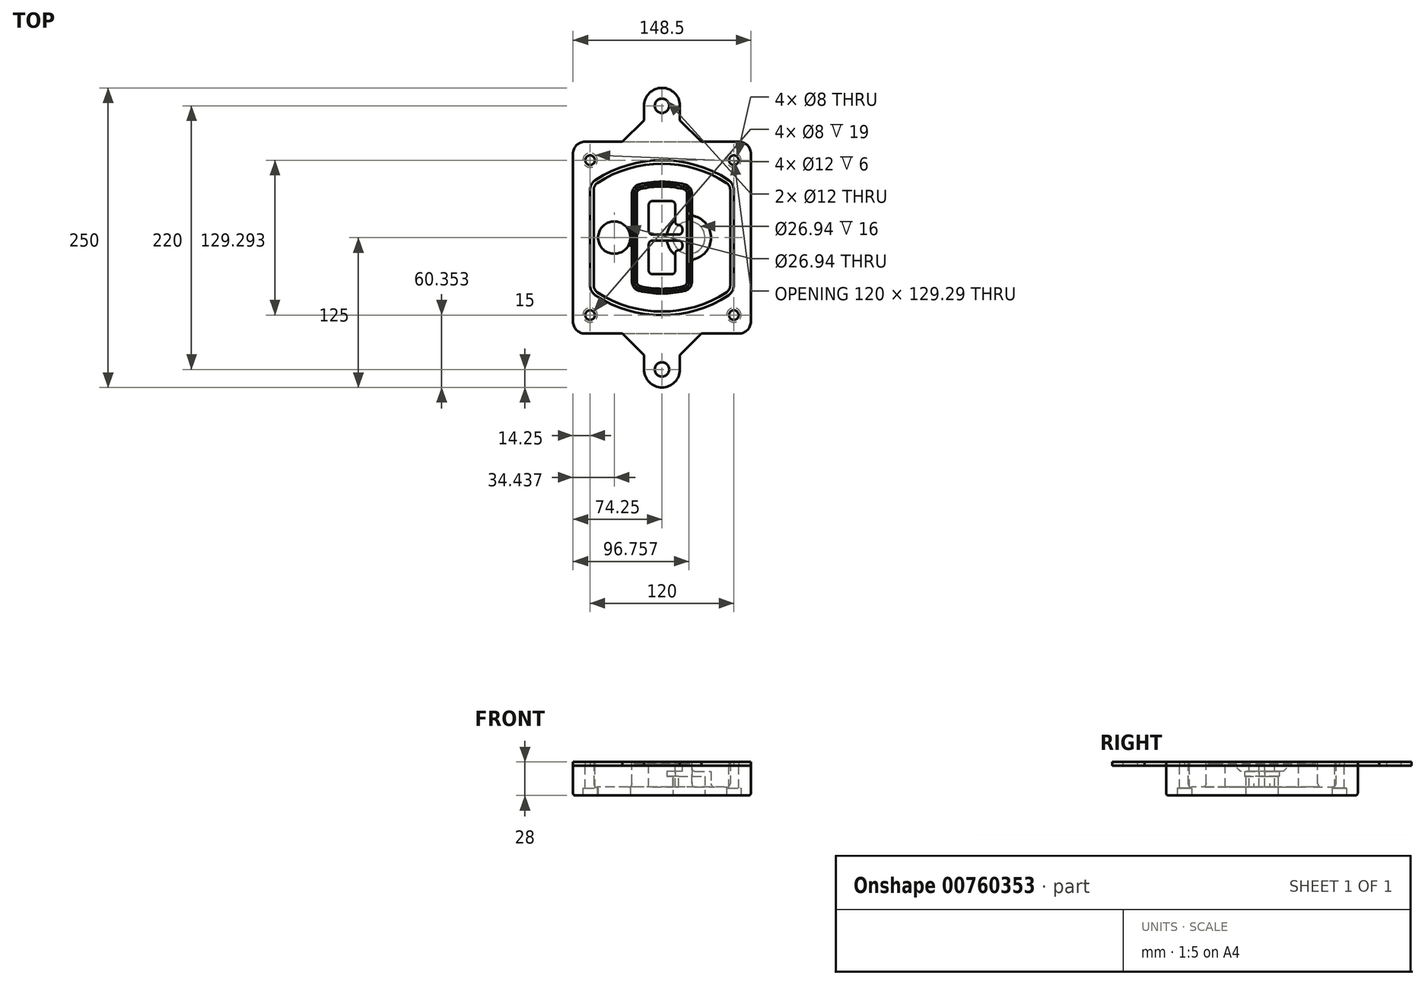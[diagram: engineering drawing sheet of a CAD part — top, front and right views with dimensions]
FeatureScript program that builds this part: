
annotation { "Feature Type Name" : "Feature", "Feature Type Description" : "" }
export const myFeature = defineFeature(function(context is Context, id is Id, definition is map)
    precondition{}
    {
        {
            var Q0;
            Q0=qCreatedBy(makeId("Top.planeOp"),FACE);
            var sketch = newSketch(context, id + "F0", { "sketchPlane" : qUnion([Q0])});
            skPoint(sketch, "E0.rect.middle", {"position": v(0, 0) * mm});
            skLineSegment(sketch, "E1.bottom", {"start": v(-64.25, -80) * mm, "end": v(64.25, -80) * mm});
            skLineSegment(sketch, "E1.top", {"start": v(-64.25, 80) * mm, "end": v(64.25, 80) * mm});
            skLineSegment(sketch, "E1.left", {"start": v(-74.25, -70) * mm, "end": v(-74.25, 70) * mm});
            skLineSegment(sketch, "E1.right", {"start": v(74.25, -70) * mm, "end": v(74.25, 70) * mm});
            skLineSegment(sketch, "E2", {"start": v(-74.25, 80) * mm, "end": v(74.25, -80) * mm, "construction": true});
            skLineSegment(sketch, "E3", {"start": v(74.25, 80) * mm, "end": v(-74.25, -80) * mm, "construction": true});
            skCircle(sketch, "E4", {"center": v(-60, 64.65) * mm, "radius": 4 * mm});
            skCircle(sketch, "E5", {"center": v(60, 64.65) * mm, "radius": 4 * mm});
            skCircle(sketch, "E6", {"center": v(60, -64.65) * mm, "radius": 4 * mm});
            skCircle(sketch, "E7", {"center": v(-60, -64.65) * mm, "radius": 4 * mm});
            skLineSegment(sketch, "E8", {"start": v(-60, 64.65) * mm, "end": v(60, 64.65) * mm, "construction": true});
            skLineSegment(sketch, "E9", {"start": v(60, 64.65) * mm, "end": v(60, -64.65) * mm, "construction": true});
            skLineSegment(sketch, "E10", {"start": v(60, -64.65) * mm, "end": v(-60, -64.65) * mm, "construction": true});
            skLineSegment(sketch, "E11", {"start": v(-60, -64.65) * mm, "end": v(-60, 64.65) * mm, "construction": true});
            skLineSegment(sketch, "E12", {"start": v(-60, 39.77) * mm, "end": v(-60, -39.77) * mm});
            skLineSegment(sketch, "E13", {"start": v(60, 39.77) * mm, "end": v(60, -39.77) * mm});
            skArc(sketch, "E14", {"start": v(55.47, 48.14) * mm, "mid": v(0, 64.65) * mm, "end": v(-55.47, 48.14) * mm});
            skArc(sketch, "E15", {"start": v(-55.47, -48.14) * mm, "mid": v(0, -64.65) * mm, "end": v(55.47, -48.14) * mm});
            skLineSegment(sketch, "E16", {"start": v(-60, 0) * mm, "end": v(60, 0) * mm, "construction": true});
            skPoint(sketch, "E17.visualSharp", {"position": v(-60, -45) * mm});
            skArc(sketch, "E17.filletArc", {"start": v(-60, -39.77) * mm, "mid": v(-58.8, -44.53) * mm, "end": v(-55.47, -48.14) * mm});
            skPoint(sketch, "E18.visualSharp", {"position": v(-60, 45) * mm});
            skArc(sketch, "E18.filletArc", {"start": v(-55.47, 48.14) * mm, "mid": v(-58.8, 44.53) * mm, "end": v(-60, 39.77) * mm});
            skPoint(sketch, "E19.visualSharp", {"position": v(60, 45) * mm});
            skArc(sketch, "E19.filletArc", {"start": v(60, 39.77) * mm, "mid": v(58.8, 44.53) * mm, "end": v(55.47, 48.14) * mm});
            skPoint(sketch, "E20.visualSharp", {"position": v(60, -45) * mm});
            skArc(sketch, "E20.filletArc", {"start": v(55.47, -48.14) * mm, "mid": v(58.8, -44.53) * mm, "end": v(60, -39.77) * mm});
            skPoint(sketch, "E21.visualSharp", {"position": v(-74.25, 80) * mm});
            skArc(sketch, "E21.filletArc", {"start": v(-64.25, 80) * mm, "mid": v(-71.32, 77.07) * mm, "end": v(-74.25, 70) * mm});
            skPoint(sketch, "E22.visualSharp", {"position": v(74.25, 80) * mm});
            skArc(sketch, "E22.filletArc", {"start": v(74.25, 70) * mm, "mid": v(71.32, 77.07) * mm, "end": v(64.25, 80) * mm});
            skPoint(sketch, "E23.visualSharp", {"position": v(74.25, -80) * mm});
            skArc(sketch, "E23.filletArc", {"start": v(64.25, -80) * mm, "mid": v(71.32, -77.07) * mm, "end": v(74.25, -70) * mm});
            skPoint(sketch, "E24.visualSharp", {"position": v(-74.25, -80) * mm});
            skArc(sketch, "E24.filletArc", {"start": v(-74.25, -70) * mm, "mid": v(-71.32, -77.07) * mm, "end": v(-64.25, -80) * mm});
            skArc(sketch, "E25.0", {"start": v(57, 39.77) * mm, "mid": v(56.16, 43.1) * mm, "end": v(53.83, 45.63) * mm});
            skLineSegment(sketch, "E25.1", {"start": v(57, 39.77) * mm, "end": v(57, -39.77) * mm});
            skArc(sketch, "E25.2", {"start": v(53.83, -45.63) * mm, "mid": v(56.16, -43.1) * mm, "end": v(57, -39.77) * mm});
            skArc(sketch, "E25.3", {"start": v(-53.83, -45.63) * mm, "mid": v(0, -61.65) * mm, "end": v(53.83, -45.63) * mm});
            skArc(sketch, "E25.4", {"start": v(-57, -39.77) * mm, "mid": v(-56.16, -43.1) * mm, "end": v(-53.83, -45.63) * mm});
            skArc(sketch, "E25.5", {"start": v(53.83, 45.63) * mm, "mid": v(0, 61.65) * mm, "end": v(-53.83, 45.63) * mm});
            skLineSegment(sketch, "E25.6", {"start": v(-57, 39.77) * mm, "end": v(-57, -39.77) * mm});
            skArc(sketch, "E25.7", {"start": v(-53.83, 45.63) * mm, "mid": v(-56.16, 43.1) * mm, "end": v(-57, 39.77) * mm});
            skArc(sketch, "E26.0", {"start": v(-57.66, 51.49) * mm, "mid": v(-62.31, 46.43) * mm, "end": v(-64, 39.77) * mm});
            skArc(sketch, "E26.1", {"start": v(57.66, 51.49) * mm, "mid": v(0, 68.65) * mm, "end": v(-57.66, 51.49) * mm});
            skArc(sketch, "E26.2", {"start": v(64, 39.77) * mm, "mid": v(62.31, 46.43) * mm, "end": v(57.66, 51.49) * mm});
            skLineSegment(sketch, "E26.3", {"start": v(64, 39.77) * mm, "end": v(64, -39.77) * mm});
            skArc(sketch, "E26.4", {"start": v(57.66, -51.49) * mm, "mid": v(62.31, -46.43) * mm, "end": v(64, -39.77) * mm});
            skLineSegment(sketch, "E26.5", {"start": v(-64, 39.77) * mm, "end": v(-64, -39.77) * mm});
            skArc(sketch, "E26.6", {"start": v(-57.66, -51.49) * mm, "mid": v(0, -68.65) * mm, "end": v(57.66, -51.49) * mm});
            skArc(sketch, "E26.7", {"start": v(-64, -39.77) * mm, "mid": v(-62.31, -46.43) * mm, "end": v(-57.66, -51.49) * mm});
            skSolve(sketch);
        }
        {
            var Q0;
            Q0=makeQuery(id+"F0.imprint","IMPRINT",FACE,{"disambiguationData":[TD([[makeQuery(id+"F0.imprint","IMPRINT",EDGE,{"derivedFrom":sQuery(id+"F0.wireOp",EDGE,"E1.bottom")}),1.0]])]});
            var Q1;
            Q1=makeQuery(id+"F0.imprint","IMPRINT",FACE,{"disambiguationData":[TD([[makeQuery(id+"F0.imprint","IMPRINT",EDGE,{"derivedFrom":sQuery(id+"F0.wireOp",EDGE,"E12")}),1.0]])]});
            var Q2;
            Q2=makeQuery(id+"F0.imprint","IMPRINT",FACE,{"disambiguationData":[TD([[makeQuery(id+"F0.imprint","IMPRINT",EDGE,{"derivedFrom":sQuery(id+"F0.wireOp",EDGE,"E25.0")}),1.0]])]});
            var Q3;
            Q3=makeQuery(id+"F0.imprint","IMPRINT",FACE,{"disambiguationData":[TD([[makeQuery(id+"F0.imprint","IMPRINT",EDGE,{"derivedFrom":sQuery(id+"F0.wireOp",EDGE,"E12")}),-1.0]])]});
            extrude(context, id + "F1", {"entities" : qUnion([Q0, Q1, Q2, Q3]), "oppositeDirection" : true, "depth" : 25 * mm});
        }
        {
            var Q0;
            Q0=makeQuery(id+"F0.imprint","IMPRINT",FACE,{"disambiguationData":[TD([[makeQuery(id+"F0.imprint","IMPRINT",EDGE,{"derivedFrom":sQuery(id+"F0.wireOp",EDGE,"E12")}),1.0]])]});
            extrude(context, id + "F2", {"entities" : qUnion([Q0]), "operationType" : NewBodyOperationType.ADD, "depth" : 3 * mm});
        }
        {
            var Q0;
            Q0=makeQuery(id+"F0.imprint","IMPRINT",FACE,{"disambiguationData":[TD([[makeQuery(id+"F0.imprint","IMPRINT",EDGE,{"derivedFrom":sQuery(id+"F0.wireOp",EDGE,"E25.0")}),1.0]])]});
            extrude(context, id + "F3", {"entities" : qUnion([Q0]), "operationType" : NewBodyOperationType.REMOVE, "oppositeDirection" : true, "depth" : 18 * mm});
        }
        {
            var Q0;
            Q0=makeQuery(id+"F2.opExtrude","CAP_FACE",FACE,{"disambiguationData":[OSD([sQuery(id+"F0.wireOp",EDGE,"E12"),sQuery(id+"F0.wireOp",EDGE,"E13"),sQuery(id+"F0.wireOp",EDGE,"E14"),sQuery(id+"F0.wireOp",EDGE,"E15"),sQuery(id+"F0.wireOp",EDGE,"E17.filletArc"),sQuery(id+"F0.wireOp",EDGE,"E18.filletArc"),sQuery(id+"F0.wireOp",EDGE,"E19.filletArc"),sQuery(id+"F0.wireOp",EDGE,"E20.filletArc"),sQuery(id+"F0.wireOp",EDGE,"E25.0"),sQuery(id+"F0.wireOp",EDGE,"E25.1"),sQuery(id+"F0.wireOp",EDGE,"E25.2"),sQuery(id+"F0.wireOp",EDGE,"E25.3"),sQuery(id+"F0.wireOp",EDGE,"E25.4"),sQuery(id+"F0.wireOp",EDGE,"E25.5"),sQuery(id+"F0.wireOp",EDGE,"E25.6"),sQuery(id+"F0.wireOp",EDGE,"E25.7")])],"isStart":false});
            var sketch = newSketch(context, id + "F4", { "sketchPlane" : qUnion([Q0])});
            skArc(sketch, "E27.0", {"start": v(-18.8, -44.5) * mm, "mid": v(0, -46.65) * mm, "end": v(18.8, -44.5) * mm});
            skArc(sketch, "E28.0", {"start": v(18.8, 44.5) * mm, "mid": v(0, 46.65) * mm, "end": v(-18.8, 44.5) * mm});
            skLineSegment(sketch, "E29", {"start": v(-25, 36.7) * mm, "end": v(-25, -36.7) * mm});
            skLineSegment(sketch, "E30", {"start": v(25, 36.7) * mm, "end": v(25, -36.7) * mm});
            skLineSegment(sketch, "E31", {"start": v(-25, 42.81) * mm, "end": v(25, 42.81) * mm, "construction": true});
            skLineSegment(sketch, "E32", {"start": v(-25, -42.81) * mm, "end": v(25, -42.81) * mm, "construction": true});
            skPoint(sketch, "E33.visualSharp", {"position": v(-25, 42.81) * mm});
            skArc(sketch, "E33.filletArc", {"start": v(-18.8, 44.5) * mm, "mid": v(-23.26, 41.69) * mm, "end": v(-25, 36.7) * mm});
            skPoint(sketch, "E34.visualSharp", {"position": v(25, 42.81) * mm});
            skArc(sketch, "E34.filletArc", {"start": v(25, 36.7) * mm, "mid": v(23.26, 41.69) * mm, "end": v(18.8, 44.5) * mm});
            skPoint(sketch, "E35.visualSharp", {"position": v(25, -42.81) * mm});
            skArc(sketch, "E35.filletArc", {"start": v(18.8, -44.5) * mm, "mid": v(23.26, -41.69) * mm, "end": v(25, -36.7) * mm});
            skPoint(sketch, "E36.visualSharp", {"position": v(-25, -42.81) * mm});
            skArc(sketch, "E36.filletArc", {"start": v(-25, -36.7) * mm, "mid": v(-23.26, -41.69) * mm, "end": v(-18.8, -44.5) * mm});
            skArc(sketch, "E37.0", {"start": v(53.83, 45.63) * mm, "mid": v(0, 61.65) * mm, "end": v(-53.83, 45.63) * mm});
            skArc(sketch, "E37.1", {"start": v(-53.83, 45.63) * mm, "mid": v(-56.16, 43.1) * mm, "end": v(-57, 39.77) * mm});
            skLineSegment(sketch, "E37.2", {"start": v(-57, 39.77) * mm, "end": v(-57, -39.77) * mm});
            skArc(sketch, "E37.3", {"start": v(-57, -39.77) * mm, "mid": v(-56.16, -43.1) * mm, "end": v(-53.83, -45.63) * mm});
            skArc(sketch, "E37.4", {"start": v(-53.83, -45.63) * mm, "mid": v(0, -61.65) * mm, "end": v(53.83, -45.63) * mm});
            skArc(sketch, "E37.5", {"start": v(53.83, -45.63) * mm, "mid": v(56.16, -43.1) * mm, "end": v(57, -39.77) * mm});
            skLineSegment(sketch, "E37.6", {"start": v(57, 39.77) * mm, "end": v(57, -39.77) * mm});
            skArc(sketch, "E37.7", {"start": v(57, 39.77) * mm, "mid": v(56.16, 43.1) * mm, "end": v(53.83, 45.63) * mm});
            skLineSegment(sketch, "E38.0", {"start": v(23, 36.7) * mm, "end": v(23, -36.7) * mm});
            skArc(sketch, "E38.1", {"start": v(18.35, -42.55) * mm, "mid": v(21.7, -40.44) * mm, "end": v(23, -36.7) * mm});
            skArc(sketch, "E38.2", {"start": v(-18.35, -42.55) * mm, "mid": v(0, -44.65) * mm, "end": v(18.35, -42.55) * mm});
            skArc(sketch, "E38.3", {"start": v(-23, -36.7) * mm, "mid": v(-21.7, -40.44) * mm, "end": v(-18.35, -42.55) * mm});
            skLineSegment(sketch, "E38.4", {"start": v(-23, 36.7) * mm, "end": v(-23, -36.7) * mm});
            skArc(sketch, "E38.5", {"start": v(23, 36.7) * mm, "mid": v(21.7, 40.44) * mm, "end": v(18.35, 42.55) * mm});
            skArc(sketch, "E38.6", {"start": v(-18.35, 42.55) * mm, "mid": v(-21.7, 40.44) * mm, "end": v(-23, 36.7) * mm});
            skArc(sketch, "E38.7", {"start": v(18.35, 42.55) * mm, "mid": v(0, 44.65) * mm, "end": v(-18.35, 42.55) * mm});
            skArc(sketch, "E39.0", {"start": v(21, 36.7) * mm, "mid": v(20.13, 39.2) * mm, "end": v(17.9, 40.6) * mm});
            skLineSegment(sketch, "E39.1", {"start": v(21, 36.7) * mm, "end": v(21, -36.7) * mm});
            skArc(sketch, "E39.2", {"start": v(17.9, -40.6) * mm, "mid": v(20.13, -39.2) * mm, "end": v(21, -36.7) * mm});
            skArc(sketch, "E39.3", {"start": v(-17.9, -40.6) * mm, "mid": v(0, -42.65) * mm, "end": v(17.9, -40.6) * mm});
            skArc(sketch, "E39.4", {"start": v(-21, -36.7) * mm, "mid": v(-20.13, -39.2) * mm, "end": v(-17.9, -40.6) * mm});
            skArc(sketch, "E39.5", {"start": v(17.9, 40.6) * mm, "mid": v(0, 42.65) * mm, "end": v(-17.9, 40.6) * mm});
            skLineSegment(sketch, "E39.6", {"start": v(-21, 36.7) * mm, "end": v(-21, -36.7) * mm});
            skArc(sketch, "E39.7", {"start": v(-17.9, 40.6) * mm, "mid": v(-20.13, 39.2) * mm, "end": v(-21, 36.7) * mm});
            skLineSegment(sketch, "E40", {"start": v(-25, 0) * mm, "end": v(25, 0) * mm, "construction": true});
            skLineSegment(sketch, "E41", {"start": v(-11, 5.5) * mm, "end": v(-11, 27.5) * mm});
            skLineSegment(sketch, "E42", {"start": v(-8, 30.5) * mm, "end": v(8, 30.5) * mm});
            skLineSegment(sketch, "E43", {"start": v(11, 27.5) * mm, "end": v(11, 13.5) * mm});
            skLineSegment(sketch, "E44", {"start": v(14, 10.5) * mm, "end": v(14, 10.5) * mm});
            skLineSegment(sketch, "E45", {"start": v(17, 7.5) * mm, "end": v(17, 5.5) * mm});
            skLineSegment(sketch, "E46", {"start": v(14, 2.5) * mm, "end": v(-8, 2.5) * mm});
            skPoint(sketch, "E47.visualSharp", {"position": v(-11, 30.5) * mm});
            skArc(sketch, "E47.filletArc", {"start": v(-8, 30.5) * mm, "mid": v(-10.12, 29.62) * mm, "end": v(-11, 27.5) * mm});
            skPoint(sketch, "E48.visualSharp", {"position": v(11, 30.5) * mm});
            skArc(sketch, "E48.filletArc", {"start": v(11, 27.5) * mm, "mid": v(10.12, 29.62) * mm, "end": v(8, 30.5) * mm});
            skPoint(sketch, "E49.visualSharp", {"position": v(11, 10.5) * mm});
            skArc(sketch, "E49.filletArc", {"start": v(11, 13.5) * mm, "mid": v(11.88, 11.38) * mm, "end": v(14, 10.5) * mm});
            skPoint(sketch, "E50.visualSharp", {"position": v(17, 10.5) * mm});
            skArc(sketch, "E50.filletArc", {"start": v(17, 7.5) * mm, "mid": v(16.12, 9.62) * mm, "end": v(14, 10.5) * mm});
            skPoint(sketch, "E51.visualSharp", {"position": v(17, 2.5) * mm});
            skArc(sketch, "E51.filletArc", {"start": v(14, 2.5) * mm, "mid": v(16.12, 3.38) * mm, "end": v(17, 5.5) * mm});
            skPoint(sketch, "E52.visualSharp", {"position": v(-11, 2.5) * mm});
            skArc(sketch, "E52.filletArc", {"start": v(-11, 5.5) * mm, "mid": v(-10.12, 3.38) * mm, "end": v(-8, 2.5) * mm});
            skLineSegment(sketch, "E53.0.MirrorCS", {"start": v(14, -2.5) * mm, "end": v(-8, -2.5) * mm});
            skArc(sketch, "E54.0.MirrorCS", {"start": v(-11, -5.5) * mm, "mid": v(-10.12, -3.38) * mm, "end": v(-8, -2.5) * mm});
            skLineSegment(sketch, "E55.0.MirrorCS", {"start": v(-11, -5.5) * mm, "end": v(-11, -27.5) * mm});
            skArc(sketch, "E56.0.MirrorCS", {"start": v(-8, -30.5) * mm, "mid": v(-10.12, -29.62) * mm, "end": v(-11, -27.5) * mm});
            skLineSegment(sketch, "E57.0.MirrorCS", {"start": v(-8, -30.5) * mm, "end": v(8, -30.5) * mm});
            skArc(sketch, "E58.0.MirrorCS", {"start": v(11, -27.5) * mm, "mid": v(10.12, -29.62) * mm, "end": v(8, -30.5) * mm});
            skLineSegment(sketch, "E59.0.MirrorCS", {"start": v(11, -27.5) * mm, "end": v(11, -13.5) * mm});
            skArc(sketch, "E60.0.MirrorCS", {"start": v(11, -13.5) * mm, "mid": v(11.88, -11.38) * mm, "end": v(14, -10.5) * mm});
            skArc(sketch, "E61.0.MirrorCS", {"start": v(17, -7.5) * mm, "mid": v(16.12, -9.62) * mm, "end": v(14, -10.5) * mm});
            skLineSegment(sketch, "E62.0.MirrorCS", {"start": v(17, -7.5) * mm, "end": v(17, -5.5) * mm});
            skArc(sketch, "E63.0.MirrorCS", {"start": v(14, -2.5) * mm, "mid": v(16.12, -3.38) * mm, "end": v(17, -5.5) * mm});
            skSolve(sketch);
        }
        {
            var Q0;
            Q0=makeQuery(id+"F4.imprint","IMPRINT",FACE,{"disambiguationData":[TD([[makeQuery(id+"F4.imprint","IMPRINT",EDGE,{"derivedFrom":sQuery(id+"F4.wireOp",EDGE,"E27.0")}),1.0]])]});
            var Q1;
            Q1=makeQuery(id+"F4.imprint","IMPRINT",FACE,{"disambiguationData":[TD([[makeQuery(id+"F4.imprint","IMPRINT",EDGE,{"derivedFrom":sQuery(id+"F4.wireOp",EDGE,"E38.0")}),-1.0]])]});
            var Q2;
            Q2=makeQuery(id+"F4.imprint","IMPRINT",FACE,{"disambiguationData":[TD([[makeQuery(id+"F4.imprint","IMPRINT",EDGE,{"derivedFrom":sQuery(id+"F4.wireOp",EDGE,"E39.0")}),1.0]])]});
            extrude(context, id + "F5", {"entities" : qUnion([Q0, Q1, Q2]), "operationType" : NewBodyOperationType.ADD, "endBound" : BoundingType.UP_TO_NEXT, "oppositeDirection" : true, "depth" : 25 * mm});
        }
        {
            var Q0;
            Q0=makeQuery(id+"F4.imprint","IMPRINT",FACE,{"disambiguationData":[TD([[makeQuery(id+"F4.imprint","IMPRINT",EDGE,{"derivedFrom":sQuery(id+"F4.wireOp",EDGE,"E38.0")}),-1.0]])]});
            extrude(context, id + "F6", {"entities" : qUnion([Q0]), "operationType" : NewBodyOperationType.REMOVE, "oppositeDirection" : true, "depth" : 2 * mm});
        }
        {
            var Q0;
            Q0=makeQuery(id+"F1.opExtrude","CAP_FACE",FACE,{"disambiguationData":[OSD([sQuery(id+"F0.wireOp",EDGE,"E1.bottom"),sQuery(id+"F0.wireOp",EDGE,"E1.top"),sQuery(id+"F0.wireOp",EDGE,"E1.left"),sQuery(id+"F0.wireOp",EDGE,"E1.right"),sQuery(id+"F0.wireOp",EDGE,"E4"),sQuery(id+"F0.wireOp",EDGE,"E5"),sQuery(id+"F0.wireOp",EDGE,"E6"),sQuery(id+"F0.wireOp",EDGE,"E7"),sQuery(id+"F0.wireOp",EDGE,"E21.filletArc"),sQuery(id+"F0.wireOp",EDGE,"E22.filletArc"),sQuery(id+"F0.wireOp",EDGE,"E23.filletArc"),sQuery(id+"F0.wireOp",EDGE,"E24.filletArc")])],"isStart":false});
            var sketch = newSketch(context, id + "F7", { "sketchPlane" : qUnion([Q0])});
            skCircle(sketch, "E64", {"center": v(22.5, 0) * mm, "radius": 13.47 * mm});
            skCircle(sketch, "E65", {"center": v(-39.81, 0) * mm, "radius": 13.47 * mm});
            skLineSegment(sketch, "E66", {"start": v(74.25, 0) * mm, "end": v(-74.25, 0) * mm});
            skCircle(sketch, "E67", {"center": v(22.5, 0) * mm, "radius": 18.47 * mm});
            skCircle(sketch, "E68", {"center": v(60, -64.65) * mm, "radius": 6 * mm});
            skCircle(sketch, "E69", {"center": v(-60, -64.65) * mm, "radius": 6 * mm});
            skCircle(sketch, "E70", {"center": v(-60, 64.65) * mm, "radius": 6 * mm});
            skCircle(sketch, "E71", {"center": v(60, 64.65) * mm, "radius": 6 * mm});
            skSolve(sketch);
        }
        {
            var Q0;
            {var subQ1=sQuery(id+"F7.wireOp",EDGE,"E66");var subQ4=sQuery(id+"F7.wireOp",EDGE,"E64");var subQ6=makeQuery(id+"F7.imprint","INTERSECT",VERTEX,{"disambiguationData":[OD(0.0)],"derivedFrom":[subQ4,subQ1]});Q0=makeQuery(id+"F7.imprint","IMPRINT",FACE,{"disambiguationData":[TD([[makeQuery(id+"F7.imprint","IMPRINT",EDGE,{"disambiguationData":[TD([[subQ6,-1.0]])],"derivedFrom":subQ4}),-1.0]])]});}
            var Q1;
            {var subQ0=sQuery(id+"F7.wireOp",EDGE,"E66");var subQ1=sQuery(id+"F7.wireOp",EDGE,"E64");var subQ3=makeQuery(id+"F7.imprint","INTERSECT",VERTEX,{"disambiguationData":[OD(0.0)],"derivedFrom":[subQ1,subQ0]});Q1=makeQuery(id+"F7.imprint","IMPRINT",FACE,{"disambiguationData":[TD([[makeQuery(id+"F7.imprint","IMPRINT",EDGE,{"disambiguationData":[TD([[subQ3,-1.0]])],"derivedFrom":subQ1}),1.0]])]});}
            var Q2;
            {var subQ0=sQuery(id+"F7.wireOp",EDGE,"E66");var subQ1=sQuery(id+"F7.wireOp",EDGE,"E64");var subQ3=makeQuery(id+"F7.imprint","INTERSECT",VERTEX,{"disambiguationData":[OD(0.0)],"derivedFrom":[subQ1,subQ0]});Q2=makeQuery(id+"F7.imprint","IMPRINT",FACE,{"disambiguationData":[TD([[makeQuery(id+"F7.imprint","IMPRINT",EDGE,{"disambiguationData":[TD([[subQ3,1.0]])],"derivedFrom":subQ1}),1.0]])]});}
            var Q3;
            {var subQ1=sQuery(id+"F7.wireOp",EDGE,"E66");var subQ4=sQuery(id+"F7.wireOp",EDGE,"E64");var subQ6=makeQuery(id+"F7.imprint","INTERSECT",VERTEX,{"disambiguationData":[OD(0.0)],"derivedFrom":[subQ4,subQ1]});Q3=makeQuery(id+"F7.imprint","IMPRINT",FACE,{"disambiguationData":[TD([[makeQuery(id+"F7.imprint","IMPRINT",EDGE,{"disambiguationData":[TD([[subQ6,1.0]])],"derivedFrom":subQ4}),-1.0]])]});}
            extrude(context, id + "F8", {"entities" : qUnion([Q0, Q1, Q2, Q3]), "operationType" : NewBodyOperationType.ADD, "oppositeDirection" : true, "depth" : 20 * mm});
        }
        {
            var Q0;
            {var subQ0=sQuery(id+"F7.wireOp",EDGE,"E66");var subQ1=sQuery(id+"F7.wireOp",EDGE,"E64");var subQ3=makeQuery(id+"F7.imprint","INTERSECT",VERTEX,{"disambiguationData":[OD(0.0)],"derivedFrom":[subQ1,subQ0]});Q0=makeQuery(id+"F7.imprint","IMPRINT",FACE,{"disambiguationData":[TD([[makeQuery(id+"F7.imprint","IMPRINT",EDGE,{"disambiguationData":[TD([[subQ3,-1.0]])],"derivedFrom":subQ1}),1.0]])]});}
            var Q1;
            {var subQ0=sQuery(id+"F7.wireOp",EDGE,"E66");var subQ1=sQuery(id+"F7.wireOp",EDGE,"E64");var subQ3=makeQuery(id+"F7.imprint","INTERSECT",VERTEX,{"disambiguationData":[OD(0.0)],"derivedFrom":[subQ1,subQ0]});Q1=makeQuery(id+"F7.imprint","IMPRINT",FACE,{"disambiguationData":[TD([[makeQuery(id+"F7.imprint","IMPRINT",EDGE,{"disambiguationData":[TD([[subQ3,1.0]])],"derivedFrom":subQ1}),1.0]])]});}
            extrude(context, id + "F9", {"entities" : qUnion([Q0, Q1]), "operationType" : NewBodyOperationType.REMOVE, "oppositeDirection" : true, "depth" : 16 * mm});
        }
        {
            var Q0;
            {var subQ0=sQuery(id+"F7.wireOp",EDGE,"E66");var subQ1=sQuery(id+"F7.wireOp",EDGE,"E65");var subQ3=makeQuery(id+"F7.imprint","INTERSECT",VERTEX,{"disambiguationData":[OD(0.0)],"derivedFrom":[subQ1,subQ0]});Q0=makeQuery(id+"F7.imprint","IMPRINT",FACE,{"disambiguationData":[TD([[makeQuery(id+"F7.imprint","IMPRINT",EDGE,{"disambiguationData":[TD([[subQ3,-1.0]])],"derivedFrom":subQ1}),1.0]])]});}
            var Q1;
            {var subQ0=sQuery(id+"F7.wireOp",EDGE,"E66");var subQ1=sQuery(id+"F7.wireOp",EDGE,"E65");var subQ3=makeQuery(id+"F7.imprint","INTERSECT",VERTEX,{"disambiguationData":[OD(0.0)],"derivedFrom":[subQ1,subQ0]});Q1=makeQuery(id+"F7.imprint","IMPRINT",FACE,{"disambiguationData":[TD([[makeQuery(id+"F7.imprint","IMPRINT",EDGE,{"disambiguationData":[TD([[subQ3,1.0]])],"derivedFrom":subQ1}),1.0]])]});}
            extrude(context, id + "F10", {"entities" : qUnion([Q0, Q1]), "operationType" : NewBodyOperationType.REMOVE, "oppositeDirection" : true, "depth" : 25 * mm});
        }
        {
            var Q0;
            Q0=makeQuery(id+"F7.imprint","IMPRINT",FACE,{"disambiguationData":[TD([[makeQuery(id+"F7.imprint","IMPRINT",EDGE,{"derivedFrom":sQuery(id+"F7.wireOp",EDGE,"E68")}),1.0]])]});
            var Q1;
            Q1=makeQuery(id+"F7.imprint","IMPRINT",FACE,{"disambiguationData":[TD([[makeQuery(id+"F7.imprint","IMPRINT",EDGE,{"derivedFrom":makeQuery(id+"F1.opExtrude","CAP_EDGE",EDGE,{"disambiguationData":[OSD([sQuery(id+"F0.wireOp",EDGE,"E5")])],"isStart":false})}),-1.0]])]});
            var Q2;
            Q2=makeQuery(id+"F7.imprint","IMPRINT",FACE,{"disambiguationData":[TD([[makeQuery(id+"F7.imprint","IMPRINT",EDGE,{"derivedFrom":sQuery(id+"F7.wireOp",EDGE,"E69")}),1.0]])]});
            var Q3;
            Q3=makeQuery(id+"F7.imprint","IMPRINT",FACE,{"disambiguationData":[TD([[makeQuery(id+"F7.imprint","IMPRINT",EDGE,{"derivedFrom":makeQuery(id+"F1.opExtrude","CAP_EDGE",EDGE,{"disambiguationData":[OSD([sQuery(id+"F0.wireOp",EDGE,"E4")])],"isStart":false})}),-1.0]])]});
            var Q4;
            Q4=makeQuery(id+"F7.imprint","IMPRINT",FACE,{"disambiguationData":[TD([[makeQuery(id+"F7.imprint","IMPRINT",EDGE,{"derivedFrom":sQuery(id+"F7.wireOp",EDGE,"E70")}),1.0]])]});
            var Q5;
            Q5=makeQuery(id+"F7.imprint","IMPRINT",FACE,{"disambiguationData":[TD([[makeQuery(id+"F7.imprint","IMPRINT",EDGE,{"derivedFrom":makeQuery(id+"F1.opExtrude","CAP_EDGE",EDGE,{"disambiguationData":[OSD([sQuery(id+"F0.wireOp",EDGE,"E7")])],"isStart":false})}),-1.0]])]});
            var Q6;
            Q6=makeQuery(id+"F7.imprint","IMPRINT",FACE,{"disambiguationData":[TD([[makeQuery(id+"F7.imprint","IMPRINT",EDGE,{"derivedFrom":sQuery(id+"F7.wireOp",EDGE,"E71")}),1.0]])]});
            var Q7;
            Q7=makeQuery(id+"F7.imprint","IMPRINT",FACE,{"disambiguationData":[TD([[makeQuery(id+"F7.imprint","IMPRINT",EDGE,{"derivedFrom":makeQuery(id+"F1.opExtrude","CAP_EDGE",EDGE,{"disambiguationData":[OSD([sQuery(id+"F0.wireOp",EDGE,"E6")])],"isStart":false})}),-1.0]])]});
            extrude(context, id + "F11", {"entities" : qUnion([Q0, Q1, Q2, Q3, Q4, Q5, Q6, Q7]), "operationType" : NewBodyOperationType.REMOVE, "oppositeDirection" : true, "depth" : 6 * mm});
        }
        {
            var Q0;
            Q0=makeQuery(id+"F9.boolean.opBoolean","COPY",FACE,{"derivedFrom":makeQuery(id+"F9.opExtrude","CAP_FACE",FACE,{"disambiguationData":[OSD([sQuery(id+"F7.wireOp",EDGE,"E64")])],"isStart":false})});
            var sketch = newSketch(context, id + "F12", { "sketchPlane" : qUnion([Q0])});
            skArc(sketch, "E72.0", {"start": v(11, 14.45) * mm, "mid": v(6.45, 9.13) * mm, "end": v(4.2, 2.5) * mm});
            skArc(sketch, "E72.1", {"start": v(4.2, -2.5) * mm, "mid": v(6.45, -9.13) * mm, "end": v(11, -14.45) * mm});
            skLineSegment(sketch, "E73", {"start": v(4.2, -2.5) * mm, "end": v(14, -2.5) * mm});
            skLineSegment(sketch, "E74.0", {"start": v(14, 2.5) * mm, "end": v(4.2, 2.5) * mm});
            skArc(sketch, "E74.1", {"start": v(14, 2.5) * mm, "mid": v(16.12, 3.38) * mm, "end": v(17, 5.5) * mm});
            skLineSegment(sketch, "E74.2", {"start": v(17, 7.5) * mm, "end": v(17, 5.5) * mm});
            skArc(sketch, "E74.3", {"start": v(17, 7.5) * mm, "mid": v(16.12, 9.62) * mm, "end": v(14, 10.5) * mm});
            skArc(sketch, "E74.4", {"start": v(11, 13.5) * mm, "mid": v(11.88, 11.38) * mm, "end": v(14, 10.5) * mm});
            skLineSegment(sketch, "E74.5", {"start": v(11, 14.45) * mm, "end": v(11, 13.5) * mm});
            skLineSegment(sketch, "E74.7", {"start": v(14, -2.5) * mm, "end": v(4.2, -2.5) * mm});
            skArc(sketch, "E74.8", {"start": v(14, -2.5) * mm, "mid": v(16.12, -3.38) * mm, "end": v(17, -5.5) * mm});
            skLineSegment(sketch, "E74.9", {"start": v(17, -7.5) * mm, "end": v(17, -5.5) * mm});
            skArc(sketch, "E74.10", {"start": v(17, -7.5) * mm, "mid": v(16.12, -9.62) * mm, "end": v(14, -10.5) * mm});
            skArc(sketch, "E74.11", {"start": v(11, -13.5) * mm, "mid": v(11.88, -11.38) * mm, "end": v(14, -10.5) * mm});
            skLineSegment(sketch, "E74.12", {"start": v(11, -14.45) * mm, "end": v(11, -13.5) * mm});
            skPoint(sketch, "E75.orphan", {"position": v(11, -27.5) * mm});
            skPoint(sketch, "E76.orphan", {"position": v(-8, -2.5) * mm});
            skPoint(sketch, "E77.orphan", {"position": v(-8, 2.5) * mm});
            skPoint(sketch, "E78.orphan", {"position": v(11, 27.5) * mm});
            skSolve(sketch);
        }
        {
            var Q0;
            {var subQ7=sQuery(id+"F12.wireOp",EDGE,"E72.0");var subQ14=sQuery(id+"F12.wireOp",EDGE,"E72.1");var subQ16=sQuery(id+"F12.wireOp",EDGE,"E74.1");var subQ18=sQuery(id+"F12.wireOp",EDGE,"E74.8");Q0=qUnion([makeQuery(id+"F12.imprint","IMPRINT",FACE,{"disambiguationData":[TD([[makeQuery(id+"F12.imprint","IMPRINT",EDGE,{"derivedFrom":subQ7}),1.0]])]}),makeQuery(id+"F12.imprint","IMPRINT",FACE,{"disambiguationData":[TD([[makeQuery(id+"F12.imprint","IMPRINT",EDGE,{"derivedFrom":subQ14}),1.0]])]}),makeQuery(id+"F12.imprint","IMPRINT",FACE,{"disambiguationData":[TD([[makeQuery(id+"F12.imprint","IMPRINT",EDGE,{"derivedFrom":subQ16}),1.0]])]}),makeQuery(id+"F12.imprint","IMPRINT",FACE,{"disambiguationData":[TD([[makeQuery(id+"F12.imprint","IMPRINT",EDGE,{"derivedFrom":subQ18}),-1.0]])]})]);}
            var Q1;
            Q1=makeQuery(id+"F5.boolean.opBoolean","SPLIT",FACE,{"disambiguationData":[TD([makeQuery(id+"F5.opExtrude","SWEPT_FACE",FACE,{"disambiguationData":[OSD([sQuery(id+"F4.wireOp",EDGE,"E41")])]})])],"derivedFrom":makeQuery(id+"F3.boolean.opBoolean","COPY",FACE,{"derivedFrom":makeQuery(id+"F3.opExtrude","CAP_FACE",FACE,{"disambiguationData":[OSD([sQuery(id+"F0.wireOp",EDGE,"E25.0"),sQuery(id+"F0.wireOp",EDGE,"E25.1"),sQuery(id+"F0.wireOp",EDGE,"E25.2"),sQuery(id+"F0.wireOp",EDGE,"E25.3"),sQuery(id+"F0.wireOp",EDGE,"E25.4"),sQuery(id+"F0.wireOp",EDGE,"E25.5"),sQuery(id+"F0.wireOp",EDGE,"E25.6"),sQuery(id+"F0.wireOp",EDGE,"E25.7")])],"isStart":false})})});
            extrude(context, id + "F13", {"entities" : qUnion([Q0]), "operationType" : NewBodyOperationType.REMOVE, "endBound" : BoundingType.UP_TO_SURFACE, "endBoundEntityFace" : qUnion([Q1]), "depth" : 25 * mm});
        }
        {
            var Q0;
            Q0=makeQuery(id+"F3.boolean.opBoolean","COPY",EDGE,{"derivedFrom":makeQuery(id+"F3.opExtrude","CAP_EDGE",EDGE,{"disambiguationData":[OSD([sQuery(id+"F0.wireOp",EDGE,"E25.6")])],"isStart":false})});
            var Q1;
            Q1=makeQuery(id+"F8.boolean.opBoolean","INTERSECT",EDGE,{"derivedFrom":[makeQuery(id+"F5.opExtrude","SWEPT_FACE",FACE,{"disambiguationData":[OSD([sQuery(id+"F4.wireOp",EDGE,"E30")])]}),makeQuery(id+"F8.opExtrude","CAP_FACE",FACE,{"disambiguationData":[OSD([sQuery(id+"F7.wireOp",EDGE,"E67")])],"isStart":false})]});
            var Q2;
            Q2=makeQuery(id+"F8.boolean.opBoolean","INTERSECT",EDGE,{"disambiguationData":[OD(1.0)],"derivedFrom":[makeQuery(id+"F5.opExtrude","SWEPT_FACE",FACE,{"disambiguationData":[OSD([sQuery(id+"F4.wireOp",EDGE,"E30")])]}),makeQuery(id+"F8.opExtrude","SWEPT_FACE",FACE,{"disambiguationData":[OSD([sQuery(id+"F7.wireOp",EDGE,"E67")])]})]});
            var Q3;
            {var subQ0=sQuery(id+"F4.wireOp",EDGE,"E30");Q3=makeQuery(id+"F8.boolean.opBoolean","SPLIT",EDGE,{"disambiguationData":[TD([makeQuery(id+"F5.opExtrude","SWEPT_FACE",FACE,{"disambiguationData":[OSD([sQuery(id+"F4.wireOp",EDGE,"E35.filletArc")])]})])],"derivedFrom":makeQuery(id+"F5.opExtrude","CAP_EDGE",EDGE,{"disambiguationData":[OSD([subQ0])],"isStart":false})});}
            var Q4;
            {var subQ0=sQuery(id+"F0.wireOp",EDGE,"E25.7");var subQ1=sQuery(id+"F0.wireOp",EDGE,"E25.1");var subQ2=sQuery(id+"F0.wireOp",EDGE,"E25.6");var subQ3=sQuery(id+"F0.wireOp",EDGE,"E25.5");var subQ4=sQuery(id+"F0.wireOp",EDGE,"E25.4");var subQ5=sQuery(id+"F0.wireOp",EDGE,"E25.0");var subQ6=sQuery(id+"F0.wireOp",EDGE,"E25.2");var subQ7=sQuery(id+"F0.wireOp",EDGE,"E25.3");Q4=makeQuery(id+"F8.boolean.opBoolean","INTERSECT",EDGE,{"derivedFrom":[makeQuery(id+"F5.boolean.opBoolean","SPLIT",FACE,{"disambiguationData":[TD([makeQuery(id+"F2.opExtrude","SWEPT_FACE",FACE,{"disambiguationData":[OSD([subQ5])]})])],"derivedFrom":makeQuery(id+"F3.boolean.opBoolean","COPY",FACE,{"derivedFrom":makeQuery(id+"F3.opExtrude","CAP_FACE",FACE,{"disambiguationData":[OSD([subQ5,subQ1,subQ6,subQ7,subQ4,subQ3,subQ2,subQ0])],"isStart":false})})}),makeQuery(id+"F8.opExtrude","SWEPT_FACE",FACE,{"disambiguationData":[OSD([sQuery(id+"F7.wireOp",EDGE,"E67")])]})]});}
            var Q5;
            Q5=makeQuery(id+"F8.boolean.opBoolean","INTERSECT",EDGE,{"disambiguationData":[OD(0.0)],"derivedFrom":[makeQuery(id+"F5.opExtrude","SWEPT_FACE",FACE,{"disambiguationData":[OSD([sQuery(id+"F4.wireOp",EDGE,"E30")])]}),makeQuery(id+"F8.opExtrude","SWEPT_FACE",FACE,{"disambiguationData":[OSD([sQuery(id+"F7.wireOp",EDGE,"E67")])]})]});
            fillet(context, id + "F14", {"entities" : qUnion([Q0, Q1, Q2, Q3, Q4, Q5]), "radius" : 3 * mm, "tangentPropagation" : true, "allowEdgeOverflow" : false});
        }
        {
            var Q0;
            Q0=makeQuery(id+"F1.opExtrude","CAP_EDGE",EDGE,{"disambiguationData":[OSD([sQuery(id+"F0.wireOp",EDGE,"E1.bottom")])],"isStart":false});
            fillet(context, id + "F15", {"entities" : qUnion([Q0]), "radius" : 2 * mm, "tangentPropagation" : true, "allowEdgeOverflow" : false});
        }
        {
            var Q0;
            {var subQ0=sQuery(id+"F0.wireOp",EDGE,"E21.filletArc");var subQ1=sQuery(id+"F0.wireOp",EDGE,"E7");var subQ2=sQuery(id+"F0.wireOp",EDGE,"E6");var subQ3=sQuery(id+"F0.wireOp",EDGE,"E5");var subQ4=sQuery(id+"F0.wireOp",EDGE,"E4");var subQ5=sQuery(id+"F0.wireOp",EDGE,"E22.filletArc");var subQ6=sQuery(id+"F0.wireOp",EDGE,"E1.bottom");var subQ7=sQuery(id+"F0.wireOp",EDGE,"E1.right");var subQ8=sQuery(id+"F0.wireOp",EDGE,"E1.top");var subQ9=sQuery(id+"F0.wireOp",EDGE,"E1.left");var subQ10=sQuery(id+"F0.wireOp",EDGE,"E23.filletArc");var subQ11=sQuery(id+"F0.wireOp",EDGE,"E24.filletArc");Q0=makeQuery(id+"F2.boolean.opBoolean","SPLIT",FACE,{"disambiguationData":[TD([makeQuery(id+"F1.opExtrude","SWEPT_FACE",FACE,{"disambiguationData":[OSD([subQ6])]})])],"derivedFrom":makeQuery(id+"F1.opExtrude","CAP_FACE",FACE,{"disambiguationData":[OSD([subQ6,subQ8,subQ9,subQ7,subQ4,subQ3,subQ2,subQ1,subQ0,subQ5,subQ10,subQ11])],"isStart":true})});}
            var sketch = newSketch(context, id + "F16", { "sketchPlane" : qUnion([Q0])});
            skLineSegment(sketch, "E79.0", {"start": v(-64.25, 80) * mm, "end": v(64.25, 80) * mm});
            skLineSegment(sketch, "E80", {"start": v(0, 80) * mm, "end": v(0, 152.2) * mm, "construction": true});
            skLineSegment(sketch, "E81", {"start": v(-33, 80) * mm, "end": v(-15, 98) * mm});
            skLineSegment(sketch, "E82", {"start": v(-15, 98) * mm, "end": v(-15, 110) * mm});
            skArc(sketch, "E83", {"start": v(15, 110) * mm, "mid": v(0, 125) * mm, "end": v(-15, 110) * mm});
            skLineSegment(sketch, "E84", {"start": v(15, 110) * mm, "end": v(15, 98) * mm});
            skLineSegment(sketch, "E85", {"start": v(15, 98) * mm, "end": v(33, 80) * mm});
            skCircle(sketch, "E86", {"center": v(0, 110) * mm, "radius": 6 * mm});
            skLineSegment(sketch, "E87", {"start": v(-90.9, 0) * mm, "end": v(103.56, 0) * mm, "construction": true});
            skLineSegment(sketch, "E88.MirrorCS", {"start": v(15, -98) * mm, "end": v(33, -80) * mm});
            skLineSegment(sketch, "E89.MirrorCS", {"start": v(15, -110) * mm, "end": v(15, -98) * mm});
            skArc(sketch, "E90.MirrorCS", {"start": v(15, -110) * mm, "mid": v(0, -125) * mm, "end": v(-15, -110) * mm});
            skLineSegment(sketch, "E91.MirrorCS", {"start": v(-15, -98) * mm, "end": v(-15, -110) * mm});
            skCircle(sketch, "E92.MirrorC", {"center": v(0, -110) * mm, "radius": 6 * mm});
            skLineSegment(sketch, "E93.MirrorCS", {"start": v(-33, -80) * mm, "end": v(-15, -98) * mm});
            skLineSegment(sketch, "E94.MirrorCS", {"start": v(0, -80) * mm, "end": v(0, -152.2) * mm, "construction": true});
            skLineSegment(sketch, "E95.MirrorCS", {"start": v(-64.25, -80) * mm, "end": v(64.25, -80) * mm});
            skLineSegment(sketch, "E96.0", {"start": v(-74.25, -70) * mm, "end": v(-74.25, 70) * mm});
            skArc(sketch, "E97.0", {"start": v(-64.25, 80) * mm, "mid": v(-71.32, 77.07) * mm, "end": v(-74.25, 70) * mm});
            skArc(sketch, "E98.0", {"start": v(-74.25, -70) * mm, "mid": v(-71.32, -77.07) * mm, "end": v(-64.25, -80) * mm});
            skArc(sketch, "E99.0", {"start": v(64.25, -80) * mm, "mid": v(71.32, -77.07) * mm, "end": v(74.25, -70) * mm});
            skLineSegment(sketch, "E100.0", {"start": v(74.25, -70) * mm, "end": v(74.25, 70) * mm});
            skArc(sketch, "E101.0", {"start": v(74.25, 70) * mm, "mid": v(71.32, 77.07) * mm, "end": v(64.25, 80) * mm});
            skArc(sketch, "E102.0", {"start": v(55.47, 48.14) * mm, "mid": v(0, 64.65) * mm, "end": v(-55.47, 48.14) * mm});
            skLineSegment(sketch, "E103.0", {"start": v(60, 39.77) * mm, "end": v(60, -39.77) * mm});
            skArc(sketch, "E104.0", {"start": v(60, 39.77) * mm, "mid": v(58.8, 44.53) * mm, "end": v(55.47, 48.14) * mm});
            skArc(sketch, "E105.0", {"start": v(-55.47, 48.14) * mm, "mid": v(-58.8, 44.53) * mm, "end": v(-60, 39.77) * mm});
            skLineSegment(sketch, "E106.0", {"start": v(-60, 39.77) * mm, "end": v(-60, -39.77) * mm});
            skArc(sketch, "E107.0", {"start": v(-60, -39.77) * mm, "mid": v(-58.8, -44.53) * mm, "end": v(-55.47, -48.14) * mm});
            skArc(sketch, "E108.0", {"start": v(-55.47, -48.14) * mm, "mid": v(0, -64.65) * mm, "end": v(55.47, -48.14) * mm});
            skCircle(sketch, "E109.0", {"center": v(60, -64.65) * mm, "radius": 4 * mm});
            skCircle(sketch, "E110.0", {"center": v(-60, -64.65) * mm, "radius": 4 * mm});
            skCircle(sketch, "E110.1", {"center": v(-60, 64.65) * mm, "radius": 4 * mm});
            skCircle(sketch, "E110.2", {"center": v(60, 64.65) * mm, "radius": 4 * mm});
            skArc(sketch, "E111.1", {"start": v(55.47, -48.14) * mm, "mid": v(58.8, -44.53) * mm, "end": v(60, -39.77) * mm});
            skSolve(sketch);
        }
        {
            var Q0;
            Q0 = qSketchRegion(id + "F16", true);
            var Q1;
            Q1=makeQuery(id+"F2.opExtrude","CAP_FACE",FACE,{"disambiguationData":[OSD([sQuery(id+"F0.wireOp",EDGE,"E12"),sQuery(id+"F0.wireOp",EDGE,"E13"),sQuery(id+"F0.wireOp",EDGE,"E14"),sQuery(id+"F0.wireOp",EDGE,"E15"),sQuery(id+"F0.wireOp",EDGE,"E17.filletArc"),sQuery(id+"F0.wireOp",EDGE,"E18.filletArc"),sQuery(id+"F0.wireOp",EDGE,"E19.filletArc"),sQuery(id+"F0.wireOp",EDGE,"E20.filletArc"),sQuery(id+"F0.wireOp",EDGE,"E25.0"),sQuery(id+"F0.wireOp",EDGE,"E25.1"),sQuery(id+"F0.wireOp",EDGE,"E25.2"),sQuery(id+"F0.wireOp",EDGE,"E25.3"),sQuery(id+"F0.wireOp",EDGE,"E25.4"),sQuery(id+"F0.wireOp",EDGE,"E25.5"),sQuery(id+"F0.wireOp",EDGE,"E25.6"),sQuery(id+"F0.wireOp",EDGE,"E25.7")])],"isStart":false});
            extrude(context, id + "F17", {"entities" : qUnion([Q0]), "endBound" : BoundingType.UP_TO_SURFACE, "depth" : 25 * mm, "endBoundEntityFace" : qUnion([Q1]), "offsetDistance" : 25 * mm});
        }
    });
